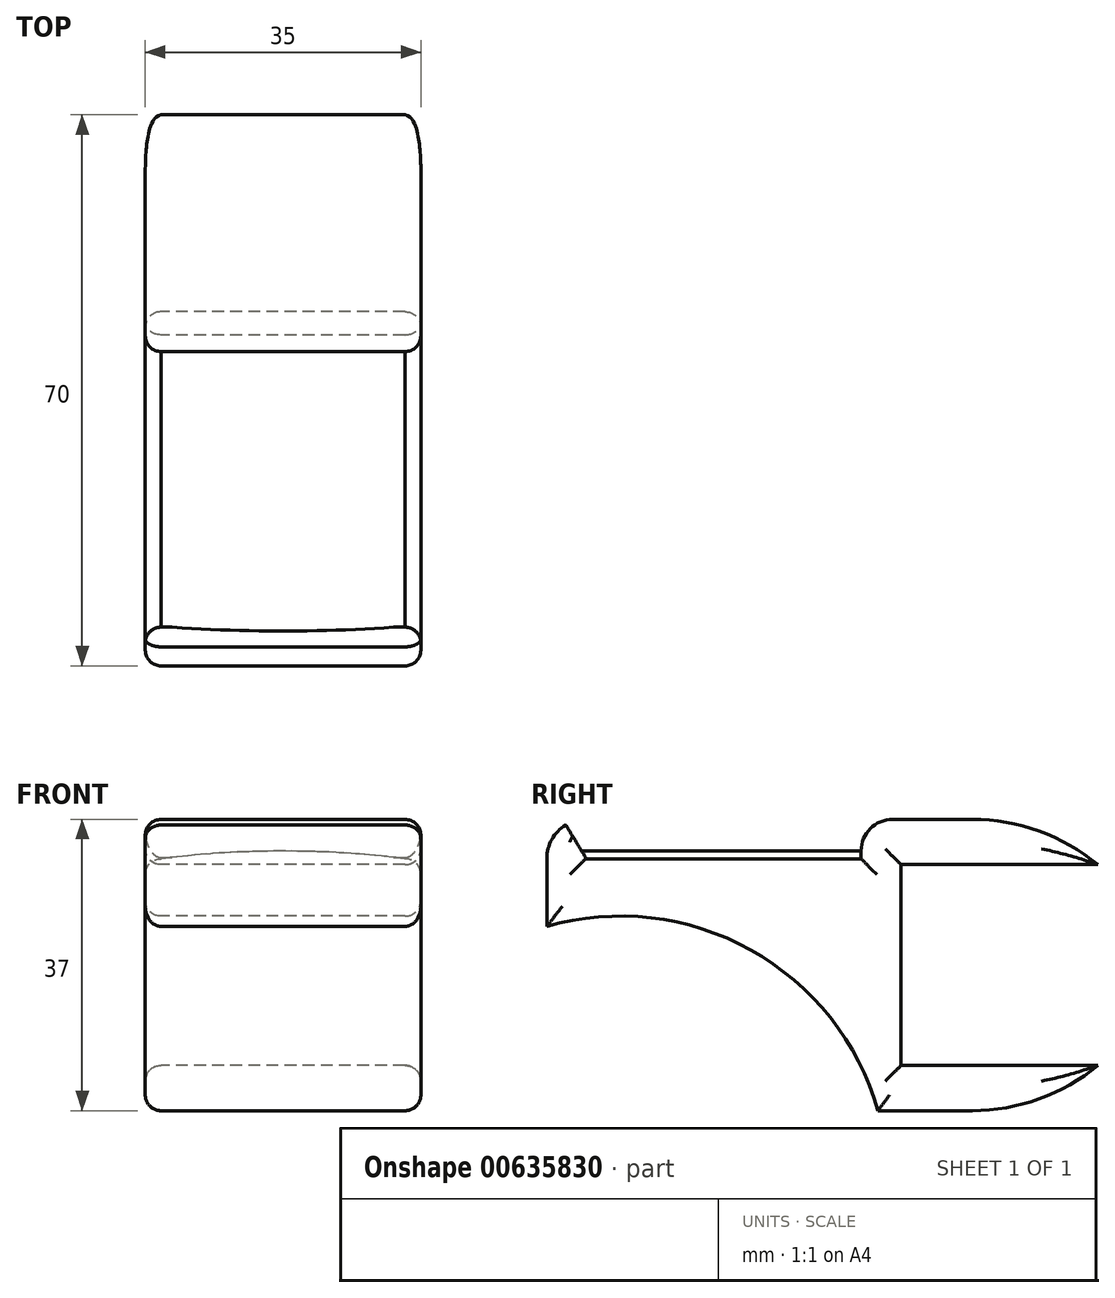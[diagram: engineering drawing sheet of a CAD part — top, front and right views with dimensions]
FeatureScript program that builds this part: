
annotation { "Feature Type Name" : "Feature", "Feature Type Description" : "" }
export const myFeature = defineFeature(function(context is Context, id is Id, definition is map)
    precondition{}
    {
        {
            var Q0;
            Q0=qCreatedBy(makeId("Top.planeOp"),FACE);
            var sketch = newSketch(context, id + "F0", { "sketchPlane" : qUnion([Q0])});
            skLineSegment(sketch, "E0.bottom", {"start": v(17.5, 35) * mm, "end": v(-17.5, 35) * mm});
            skLineSegment(sketch, "E0.top", {"start": v(17.5, -35) * mm, "end": v(-17.5, -35) * mm});
            skLineSegment(sketch, "E0.left", {"start": v(17.5, 35) * mm, "end": v(17.5, -35) * mm});
            skLineSegment(sketch, "E0.right", {"start": v(-17.5, 35) * mm, "end": v(-17.5, -35) * mm});
            skPoint(sketch, "E0.middle", {"position": v(0, 0) * mm});
            skSolve(sketch);
        }
        {
            var Q0;
            Q0=makeQuery(id+"F0.imprint","IMPRINT",FACE,{"disambiguationData":[TD([[makeQuery(id+"F0.imprint","IMPRINT",EDGE,{"derivedFrom":sQuery(id+"F0.wireOp",EDGE,"E0.bottom")}),1.0]])]});
            extrude(context, id + "F1", {"entities" : qUnion([Q0]), "depth" : 37 * mm, "offsetDistance" : 25 * mm});
        }
        {
            var Q0;
            Q0=makeQuery(id+"F1.opExtrude","SWEPT_FACE",FACE,{"disambiguationData":[OSD([sQuery(id+"F0.wireOp",EDGE,"E0.bottom")])]});
            var sketch = newSketch(context, id + "F2", { "sketchPlane" : qUnion([Q0])});
            skLineSegment(sketch, "E1.bottom", {"start": v(-17.5, 31.25) * mm, "end": v(17.5, 31.25) * mm});
            skLineSegment(sketch, "E1.top", {"start": v(-17.5, 5.75) * mm, "end": v(17.5, 5.75) * mm});
            skLineSegment(sketch, "E1.left", {"start": v(-17.5, 31.25) * mm, "end": v(-17.5, 5.75) * mm});
            skLineSegment(sketch, "E1.right", {"start": v(17.5, 31.25) * mm, "end": v(17.5, 5.75) * mm});
            skPoint(sketch, "E2", {"position": v(0, 18.5) * mm});
            skPoint(sketch, "E2.positionSnap0", {"position": v(0, 37) * mm});
            skPoint(sketch, "E3", {"position": v(0, 0) * mm});
            skPoint(sketch, "E4", {"position": v(0, 31.25) * mm});
            skPoint(sketch, "E5", {"position": v(0, 5.75) * mm});
            skLineSegment(sketch, "E6", {"start": v(0, 31.25) * mm, "end": v(0, 5.75) * mm, "construction": true});
            skSolve(sketch);
        }
        {
            var Q0;
            Q0=makeQuery(id+"F2.imprint","IMPRINT",FACE,{"disambiguationData":[TD([[makeQuery(id+"F2.imprint","IMPRINT",EDGE,{"derivedFrom":sQuery(id+"F2.wireOp",EDGE,"E1.bottom")}),-1.0]])]});
            extrude(context, id + "F3", {"entities" : qUnion([Q0]), "operationType" : NewBodyOperationType.REMOVE, "oppositeDirection" : true, "depth" : 25 * mm, "offsetDistance" : 25 * mm});
        }
        {
            var Q0;
            Q0=makeQuery(id+"F1.opExtrude","CAP_FACE",FACE,{"disambiguationData":[OSD([sQuery(id+"F0.wireOp",EDGE,"E0.bottom"),sQuery(id+"F0.wireOp",EDGE,"E0.top"),sQuery(id+"F0.wireOp",EDGE,"E0.left"),sQuery(id+"F0.wireOp",EDGE,"E0.right")])],"isStart":false});
            var sketch = newSketch(context, id + "F4", { "sketchPlane" : qUnion([Q0])});
            skLineSegment(sketch, "E7.bottom", {"start": v(-17.5, 4.93) * mm, "end": v(17.5, 4.93) * mm});
            skLineSegment(sketch, "E7.top", {"start": v(-17.5, -30.07) * mm, "end": v(17.5, -30.07) * mm});
            skLineSegment(sketch, "E7.left", {"start": v(-17.5, 4.93) * mm, "end": v(-17.5, -30.07) * mm});
            skLineSegment(sketch, "E7.right", {"start": v(17.5, 4.93) * mm, "end": v(17.5, -30.07) * mm});
            skSolve(sketch);
        }
        {
            var Q0;
            Q0 = qSketchRegion(id + "F4", true);
            extrude(context, id + "F5", {"entities" : qUnion([Q0]), "operationType" : NewBodyOperationType.REMOVE, "oppositeDirection" : true, "depth" : 5 * mm, "offsetDistance" : 25 * mm});
        }
        {
            var Q0;
            Q0=makeQuery(id+"F1.opExtrude","CAP_EDGE",EDGE,{"disambiguationData":[OSD([sQuery(id+"F0.wireOp",EDGE,"E0.bottom")])],"isStart":false});
            var Q1;
            Q1=makeQuery(id+"F1.opExtrude","CAP_EDGE",EDGE,{"disambiguationData":[OSD([sQuery(id+"F0.wireOp",EDGE,"E0.bottom")])],"isStart":true});
            fillet(context, id + "F6", {"entities" : qUnion([Q0, Q1]), "radius" : 25 * mm, "tangentPropagation" : true, "allowEdgeOverflow" : false});
        }
        {
            var Q0;
            Q0=makeQuery(id+"F1.opExtrude","SWEPT_FACE",FACE,{"disambiguationData":[OSD([sQuery(id+"F0.wireOp",EDGE,"E0.right")])]});
            var sketch = newSketch(context, id + "F7", { "sketchPlane" : qUnion([Q0])});
            skLineSegment(sketch, "E8", {"start": v(35, 23.4) * mm, "end": v(35, 0) * mm});
            skLineSegment(sketch, "E9", {"start": v(35, 0) * mm, "end": v(-7.06, 0) * mm});
            skArc(sketch, "E10", {"start": v(35, 23.4) * mm, "mid": v(9.11, 20.43) * mm, "end": v(-7.06, 0) * mm});
            skSolve(sketch);
        }
        {
            var Q0;
            Q0=makeQuery(id+"F7.imprint","IMPRINT",FACE,{"disambiguationData":[TD([[makeQuery(id+"F7.imprint","IMPRINT",EDGE,{"derivedFrom":sQuery(id+"F7.wireOp",EDGE,"E8")}),-1.0]])]});
            extrude(context, id + "F8", {"entities" : qUnion([Q0]), "operationType" : NewBodyOperationType.REMOVE, "oppositeDirection" : true, "depth" : 50 * mm, "offsetDistance" : 25 * mm});
        }
        {
            var Q0;
            Q0=makeQuery(id+"F8.boolean.opBoolean","COPY",EDGE,{"derivedFrom":makeQuery(id+"F8.opExtrude","SWEPT_EDGE",EDGE,{"disambiguationData":[OSD([sQuery(id+"F0.wireOp",EDGE,"E0.top"),sQuery(id+"F0.wireOp",EDGE,"E0.right"),sQuery(id+"F7.wireOp",EDGE,"E8"),sQuery(id+"F7.wireOp",EDGE,"E10")])]})});
            var Q1;
            Q1=makeQuery(id+"F8.boolean.opBoolean","COPY",EDGE,{"derivedFrom":makeQuery(id+"F8.opExtrude","SWEPT_EDGE",EDGE,{"disambiguationData":[OSD([sQuery(id+"F0.wireOp",EDGE,"E0.right"),sQuery(id+"F7.wireOp",EDGE,"E9"),sQuery(id+"F7.wireOp",EDGE,"E10")])]})});
            var Q2;
            Q2=makeQuery(id+"F1.opExtrude","CAP_EDGE",EDGE,{"disambiguationData":[OSD([sQuery(id+"F0.wireOp",EDGE,"E0.top")])],"isStart":false});
            fillet(context, id + "F9", {"entities" : qUnion([Q0, Q1, Q2]), "radius" : 5 * mm, "tangentPropagation" : true, "allowEdgeOverflow" : false});
        }
        {
            var Q0;
            Q0=makeQuery(id+"F1.opExtrude","SWEPT_FACE",FACE,{"disambiguationData":[OSD([sQuery(id+"F0.wireOp",EDGE,"E0.right")])]});
            var Q1;
            Q1=makeQuery(id+"F1.opExtrude","SWEPT_FACE",FACE,{"disambiguationData":[OSD([sQuery(id+"F0.wireOp",EDGE,"E0.left")])]});
            fillet(context, id + "F10", {"entities" : qUnion([Q0, Q1]), "radius" : 2 * mm, "tangentPropagation" : true, "allowEdgeOverflow" : false});
        }
        {
            var Q0;
            Q0=makeQuery(id+"F9.opFillet","BLEND_EDGE",EDGE,{"blendedFrom":[makeQuery(id+"F1.opExtrude","CAP_EDGE",EDGE,{"disambiguationData":[OSD([sQuery(id+"F0.wireOp",EDGE,"E0.top")])],"isStart":false}),makeQuery(id+"F5.boolean.opBoolean","COPY",FACE,{"derivedFrom":makeQuery(id+"F5.opExtrude","SWEPT_FACE",FACE,{"disambiguationData":[OSD([sQuery(id+"F4.wireOp",EDGE,"E7.top")])]})})],"blendedInto":[makeQuery(id+"F5.boolean.opBoolean","COPY",FACE,{"derivedFrom":makeQuery(id+"F5.opExtrude","SWEPT_FACE",FACE,{"disambiguationData":[OSD([sQuery(id+"F4.wireOp",EDGE,"E7.top")])]})})]});
            chamfer(context, id + "F11", {"entities" : qUnion([Q0]), "chamferType" : ChamferType.OFFSET_ANGLE, "width" : 4.8 * mm, "oppositeDirection" : false, "angle" : 1.2 * degree});
        }
        {
            var Q0;
            Q0=makeQuery(id+"F5.boolean.opBoolean","COPY",EDGE,{"derivedFrom":makeQuery(id+"F5.opExtrude","CAP_EDGE",EDGE,{"disambiguationData":[OSD([sQuery(id+"F4.wireOp",EDGE,"E7.bottom")])],"isStart":true})});
            fillet(context, id + "F12", {"entities" : qUnion([Q0]), "radius" : 4 * mm, "tangentPropagation" : true, "allowEdgeOverflow" : false});
        }
        {
            var Q0;
            Q0=makeQuery(id+"F5.boolean.opBoolean","COPY",FACE,{"derivedFrom":makeQuery(id+"F5.opExtrude","SWEPT_FACE",FACE,{"disambiguationData":[OSD([sQuery(id+"F4.wireOp",EDGE,"E7.bottom")])]})});
            var sketch = newSketch(context, id + "F13", { "sketchPlane" : qUnion([Q0])});
            skArc(sketch, "E11", {"start": v(15.5, 32) * mm, "mid": v(0, 32.98) * mm, "end": v(-15.5, 32) * mm});
            skLineSegment(sketch, "E12", {"start": v(15.5, 32) * mm, "end": v(-15.5, 32) * mm});
            skSolve(sketch);
        }
        {
            var Q0;
            Q0 = qSketchRegion(id + "F13", true);
            extrude(context, id + "F14", {"entities" : qUnion([Q0]), "operationType" : NewBodyOperationType.ADD, "depth" : 36.2 * mm, "offsetDistance" : 25 * mm});
        }
    });
